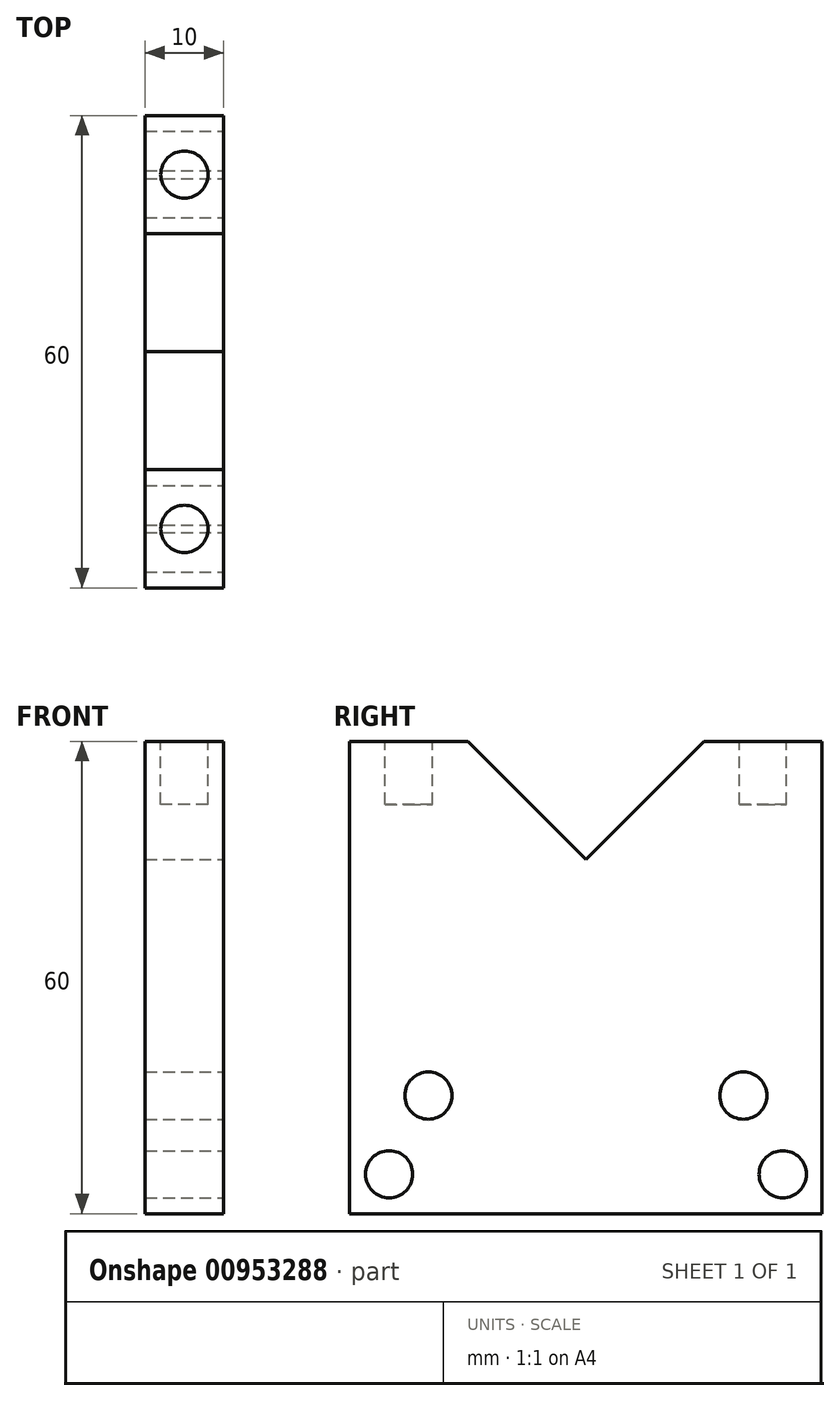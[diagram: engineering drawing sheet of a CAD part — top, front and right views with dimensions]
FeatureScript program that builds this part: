
annotation { "Feature Type Name" : "Feature", "Feature Type Description" : "" }
export const myFeature = defineFeature(function(context is Context, id is Id, definition is map)
    precondition{}
    {
        {
            var Q0;
            Q0=qCreatedBy(makeId("Right.planeOp"),FACE);
            var sketch = newSketch(context, id + "F0", { "sketchPlane" : qUnion([Q0])});
            skLineSegment(sketch, "E0.top", {"start": v(-30, 0) * mm, "end": v(30, 0) * mm});
            skLineSegment(sketch, "E0.left", {"start": v(-30, 60) * mm, "end": v(-30, 0) * mm});
            skLineSegment(sketch, "E0.right", {"start": v(30, 60) * mm, "end": v(30, 0) * mm});
            skLineSegment(sketch, "E1", {"start": v(-30, 60) * mm, "end": v(-15, 60) * mm});
            skLineSegment(sketch, "E2", {"start": v(-15, 60) * mm, "end": v(0, 45) * mm});
            skLineSegment(sketch, "E3", {"start": v(0, 45) * mm, "end": v(15, 60) * mm});
            skLineSegment(sketch, "E4", {"start": v(15, 60) * mm, "end": v(30, 60) * mm});
            skCircle(sketch, "E5", {"center": v(-20, 15) * mm, "radius": 3 * mm});
            skCircle(sketch, "E6", {"center": v(20, 15) * mm, "radius": 3 * mm});
            skCircle(sketch, "E7", {"center": v(-25, 5) * mm, "radius": 3 * mm});
            skCircle(sketch, "E8", {"center": v(25, 5) * mm, "radius": 3 * mm});
            skSolve(sketch);
        }
        {
            var Q0;
            Q0 = qSketchRegion(id + "F0", true);
            extrude(context, id + "F1", {"entities" : qUnion([Q0]), "oppositeDirection" : true, "depth" : 10 * mm, "offsetDistance" : 25 * mm});
        }
        {
            var Q0;
            Q0=makeQuery(id+"F1.opExtrude","SWEPT_FACE",FACE,{"disambiguationData":[OSD([sQuery(id+"F0.wireOp",EDGE,"E1")])]});
            var sketch = newSketch(context, id + "F2", { "sketchPlane" : qUnion([Q0])});
            skCircle(sketch, "E9", {"center": v(-5, -22.5) * mm, "radius": 3 * mm});
            skPoint(sketch, "E9.centerSnap0", {"position": v(0, -22.5) * mm});
            skPoint(sketch, "E9.centerSnap1", {"position": v(-5, -15) * mm});
            skSolve(sketch);
        }
        {
            var Q0;
            Q0=makeQuery(id+"F1.opExtrude","SWEPT_FACE",FACE,{"disambiguationData":[OSD([sQuery(id+"F0.wireOp",EDGE,"E4")])]});
            var sketch = newSketch(context, id + "F3", { "sketchPlane" : qUnion([Q0])});
            skCircle(sketch, "E10", {"center": v(-5, 22.5) * mm, "radius": 3 * mm});
            skPoint(sketch, "E10.centerSnap0", {"position": v(0, 22.5) * mm});
            skPoint(sketch, "E10.centerSnap1", {"position": v(-5, 30) * mm});
            skSolve(sketch);
        }
        {
            var Q0;
            Q0 = qSketchRegion(id + "F2", true);
            var Q1;
            Q1 = qSketchRegion(id + "F3", true);
            extrude(context, id + "F4", {"entities" : qUnion([Q0, Q1]), "operationType" : NewBodyOperationType.REMOVE, "oppositeDirection" : true, "depth" : 8 * mm, "offsetDistance" : 25 * mm});
        }
    });
